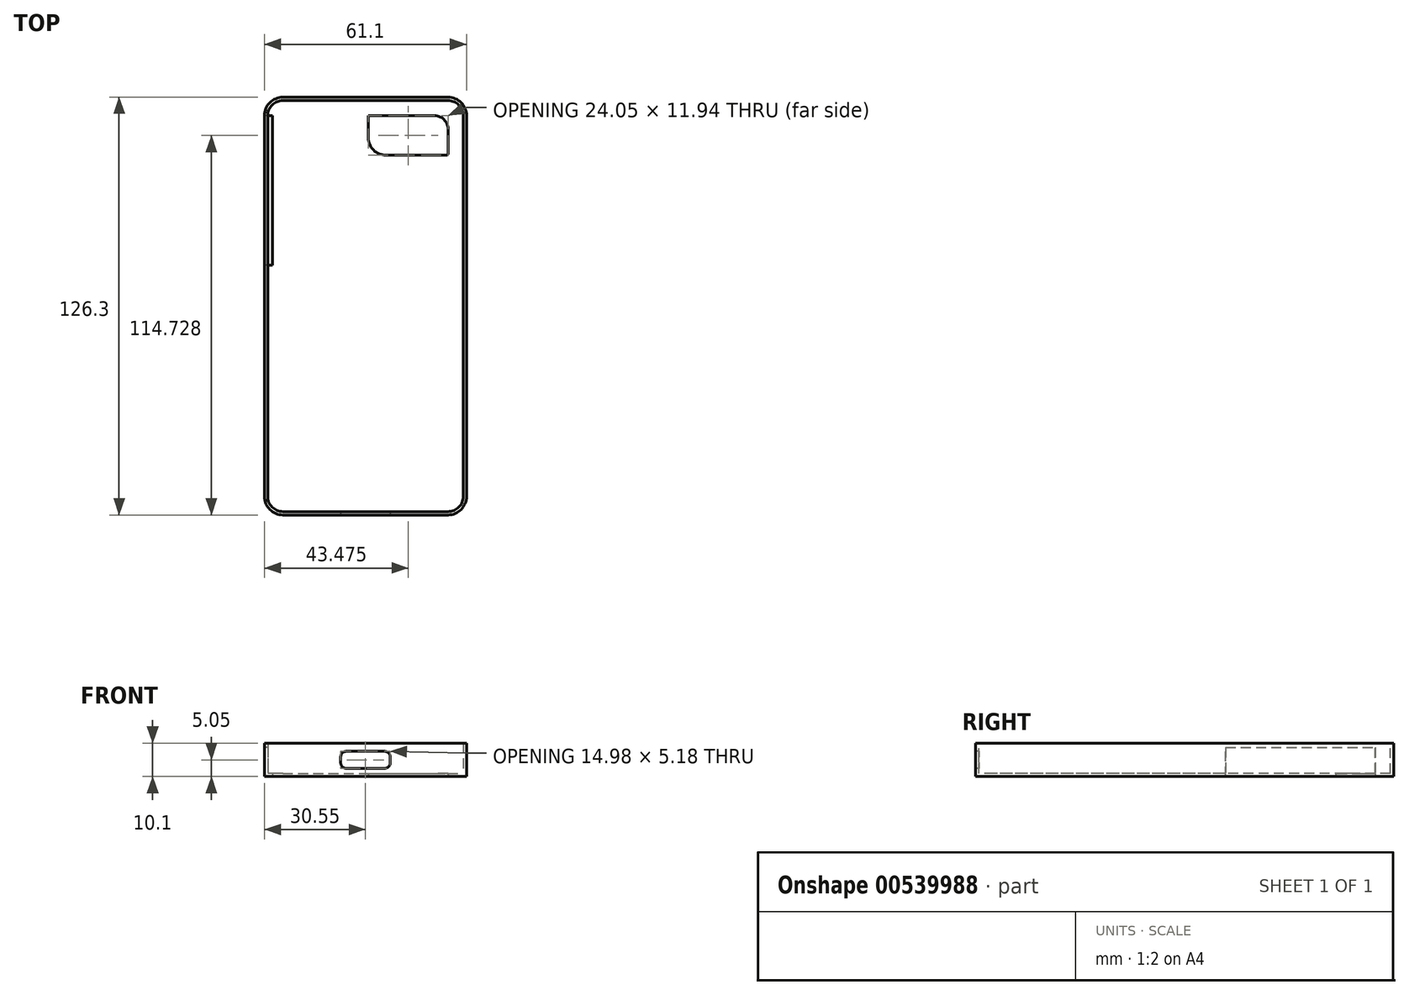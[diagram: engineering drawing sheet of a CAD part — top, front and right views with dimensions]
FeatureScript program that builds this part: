
annotation { "Feature Type Name" : "Feature", "Feature Type Description" : "" }
export const myFeature = defineFeature(function(context is Context, id is Id, definition is map)
    precondition{}
    {
        {
            var Q0;
            Q0=qCreatedBy(makeId("Top.planeOp"),FACE);
            var sketch = newSketch(context, id + "F0", { "sketchPlane" : qUnion([Q0])});
            skLineSegment(sketch, "E0.bottom", {"start": v(-24.95, 63.15) * mm, "end": v(24.95, 63.15) * mm});
            skLineSegment(sketch, "E0.top", {"start": v(-24.95, -63.15) * mm, "end": v(24.95, -63.15) * mm});
            skLineSegment(sketch, "E0.left", {"start": v(-30.55, 57.55) * mm, "end": v(-30.55, -57.55) * mm});
            skLineSegment(sketch, "E0.right", {"start": v(30.55, 57.55) * mm, "end": v(30.55, -57.55) * mm});
            skPoint(sketch, "E0.middle", {"position": v(0, 0) * mm});
            skPoint(sketch, "E1.visualSharp", {"position": v(30.55, 63.15) * mm});
            skArc(sketch, "E1.filletArc", {"start": v(30.55, 57.55) * mm, "mid": v(28.9, 61.5) * mm, "end": v(24.95, 63.15) * mm});
            skPoint(sketch, "E2.visualSharp", {"position": v(-30.55, 63.15) * mm});
            skArc(sketch, "E2.filletArc", {"start": v(-24.95, 63.15) * mm, "mid": v(-28.9, 61.5) * mm, "end": v(-30.55, 57.55) * mm});
            skPoint(sketch, "E3.visualSharp", {"position": v(-30.55, -63.15) * mm});
            skArc(sketch, "E3.filletArc", {"start": v(-30.55, -57.55) * mm, "mid": v(-28.9, -61.5) * mm, "end": v(-24.95, -63.15) * mm});
            skPoint(sketch, "E4.visualSharp", {"position": v(30.55, -63.15) * mm});
            skArc(sketch, "E4.filletArc", {"start": v(24.95, -63.15) * mm, "mid": v(28.9, -61.5) * mm, "end": v(30.55, -57.55) * mm});
            skSolve(sketch);
        }
        {
            var Q0;
            Q0 = qSketchRegion(id + "F0", true);
            extrude(context, id + "F1", {"entities" : qUnion([Q0]), "depth" : (7.6 + 2.5) * mm, "offsetDistance" : 25 * mm});
        }
        {
            var Q0;
            Q0=makeQuery(id+"F1.opExtrude","CAP_FACE",FACE,{"disambiguationData":[OSD([sQuery(id+"F0.wireOp",EDGE,"E0.bottom"),sQuery(id+"F0.wireOp",EDGE,"E0.top"),sQuery(id+"F0.wireOp",EDGE,"E0.left"),sQuery(id+"F0.wireOp",EDGE,"E0.right"),sQuery(id+"F0.wireOp",EDGE,"E1.filletArc"),sQuery(id+"F0.wireOp",EDGE,"E2.filletArc"),sQuery(id+"F0.wireOp",EDGE,"E3.filletArc"),sQuery(id+"F0.wireOp",EDGE,"E4.filletArc")])],"isStart":false});
            shell(context, id + "F2", {"entities" : qUnion([Q0]), "thickness" : 1 * mm});
        }
        {
            var Q0;
            Q0=makeQuery(id+"F1.opExtrude","CAP_FACE",FACE,{"disambiguationData":[OSD([sQuery(id+"F0.wireOp",EDGE,"E0.bottom"),sQuery(id+"F0.wireOp",EDGE,"E0.top"),sQuery(id+"F0.wireOp",EDGE,"E0.left"),sQuery(id+"F0.wireOp",EDGE,"E0.right"),sQuery(id+"F0.wireOp",EDGE,"E1.filletArc"),sQuery(id+"F0.wireOp",EDGE,"E2.filletArc"),sQuery(id+"F0.wireOp",EDGE,"E3.filletArc"),sQuery(id+"F0.wireOp",EDGE,"E4.filletArc")])],"isStart":true});
            var sketch = newSketch(context, id + "F3", { "sketchPlane" : qUnion([Q0])});
            skLineSegment(sketch, "E5.bottom", {"start": v(20.95, -57.55) * mm, "end": v(0.9, -57.55) * mm});
            skLineSegment(sketch, "E5.top", {"start": v(24.55, -45.6) * mm, "end": v(6.2, -45.6) * mm});
            skLineSegment(sketch, "E5.left", {"start": v(24.95, -53.55) * mm, "end": v(24.95, -46) * mm});
            skLineSegment(sketch, "E5.right", {"start": v(0.9, -57.55) * mm, "end": v(0.9, -50.9) * mm});
            skPoint(sketch, "E6.visualSharp", {"position": v(24.95, -57.55) * mm});
            skArc(sketch, "E6.filletArc", {"start": v(20.95, -57.55) * mm, "mid": v(23.78, -56.38) * mm, "end": v(24.95, -53.55) * mm});
            skPoint(sketch, "E7.visualSharp", {"position": v(24.95, -45.6) * mm});
            skArc(sketch, "E7.filletArc", {"start": v(24.95, -46) * mm, "mid": v(24.83, -45.72) * mm, "end": v(24.55, -45.6) * mm});
            skPoint(sketch, "E8.visualSharp", {"position": v(0.9, -45.6) * mm});
            skArc(sketch, "E8.filletArc", {"start": v(6.2, -45.6) * mm, "mid": v(2.45, -47.16) * mm, "end": v(0.9, -50.9) * mm});
            skSolve(sketch);
        }
        {
            var Q0;
            Q0 = qSketchRegion(id + "F3", true);
            extrude(context, id + "F4", {"entities" : qUnion([Q0]), "operationType" : NewBodyOperationType.REMOVE, "oppositeDirection" : true, "depth" : 25 * mm, "offsetDistance" : 25 * mm});
        }
        {
            var Q0;
            Q0=makeQuery(id+"F1.opExtrude","SWEPT_FACE",FACE,{"disambiguationData":[OSD([sQuery(id+"F0.wireOp",EDGE,"E0.left")])]});
            var sketch = newSketch(context, id + "F5", { "sketchPlane" : qUnion([Q0])});
            skLineSegment(sketch, "E9.bottom", {"start": v(-57.55, 0) * mm, "end": v(-12.38, 0) * mm});
            skLineSegment(sketch, "E9.top", {"start": v(-57.55, 8.8) * mm, "end": v(-12.38, 8.8) * mm});
            skLineSegment(sketch, "E9.left", {"start": v(-57.55, 0) * mm, "end": v(-57.55, 8.8) * mm});
            skLineSegment(sketch, "E9.right", {"start": v(-12.38, 0) * mm, "end": v(-12.38, 8.8) * mm});
            skSolve(sketch);
        }
        {
            var Q0;
            Q0 = qSketchRegion(id + "F5", true);
            extrude(context, id + "F6", {"entities" : qUnion([Q0]), "operationType" : NewBodyOperationType.REMOVE, "oppositeDirection" : true, "depth" : 2.5 * mm, "offsetDistance" : 25 * mm});
        }
        {
            var Q0;
            Q0=makeQuery(id+"F1.opExtrude","SWEPT_FACE",FACE,{"disambiguationData":[OSD([sQuery(id+"F0.wireOp",EDGE,"E0.top")])]});
            var sketch = newSketch(context, id + "F7", { "sketchPlane" : qUnion([Q0])});
            skLineSegment(sketch, "E10.bottom", {"start": v(-5.74, 7.64) * mm, "end": v(5.74, 7.64) * mm});
            skLineSegment(sketch, "E10.top", {"start": v(-5.74, 2.46) * mm, "end": v(5.74, 2.46) * mm});
            skLineSegment(sketch, "E10.left", {"start": v(-7.49, 5.89) * mm, "end": v(-7.49, 4.21) * mm});
            skLineSegment(sketch, "E10.right", {"start": v(7.49, 5.89) * mm, "end": v(7.49, 4.21) * mm});
            skPoint(sketch, "E10.middle", {"position": v(0, 5.05) * mm});
            skPoint(sketch, "E10.middle.positionSnap0", {"position": v(24.95, 5.05) * mm});
            skPoint(sketch, "E10.centerSnap0", {"position": v(24.95, 5.05) * mm});
            skPoint(sketch, "E11.visualSharp", {"position": v(7.49, 7.64) * mm});
            skArc(sketch, "E11.filletArc", {"start": v(7.49, 5.89) * mm, "mid": v(6.98, 7.13) * mm, "end": v(5.74, 7.64) * mm});
            skPoint(sketch, "E12.visualSharp", {"position": v(7.49, 2.46) * mm});
            skArc(sketch, "E12.filletArc", {"start": v(5.74, 2.46) * mm, "mid": v(6.98, 2.97) * mm, "end": v(7.49, 4.21) * mm});
            skPoint(sketch, "E13.visualSharp", {"position": v(-7.49, 2.46) * mm});
            skArc(sketch, "E13.filletArc", {"start": v(-7.49, 4.21) * mm, "mid": v(-6.98, 2.97) * mm, "end": v(-5.74, 2.46) * mm});
            skPoint(sketch, "E14.visualSharp", {"position": v(-7.49, 7.64) * mm});
            skArc(sketch, "E14.filletArc", {"start": v(-5.74, 7.64) * mm, "mid": v(-6.98, 7.13) * mm, "end": v(-7.49, 5.89) * mm});
            skSolve(sketch);
        }
        {
            var Q0;
            Q0 = qSketchRegion(id + "F7", true);
            extrude(context, id + "F8", {"entities" : qUnion([Q0]), "operationType" : NewBodyOperationType.REMOVE, "oppositeDirection" : true, "depth" : 2.5 * mm, "offsetDistance" : 25 * mm});
        }
    });
